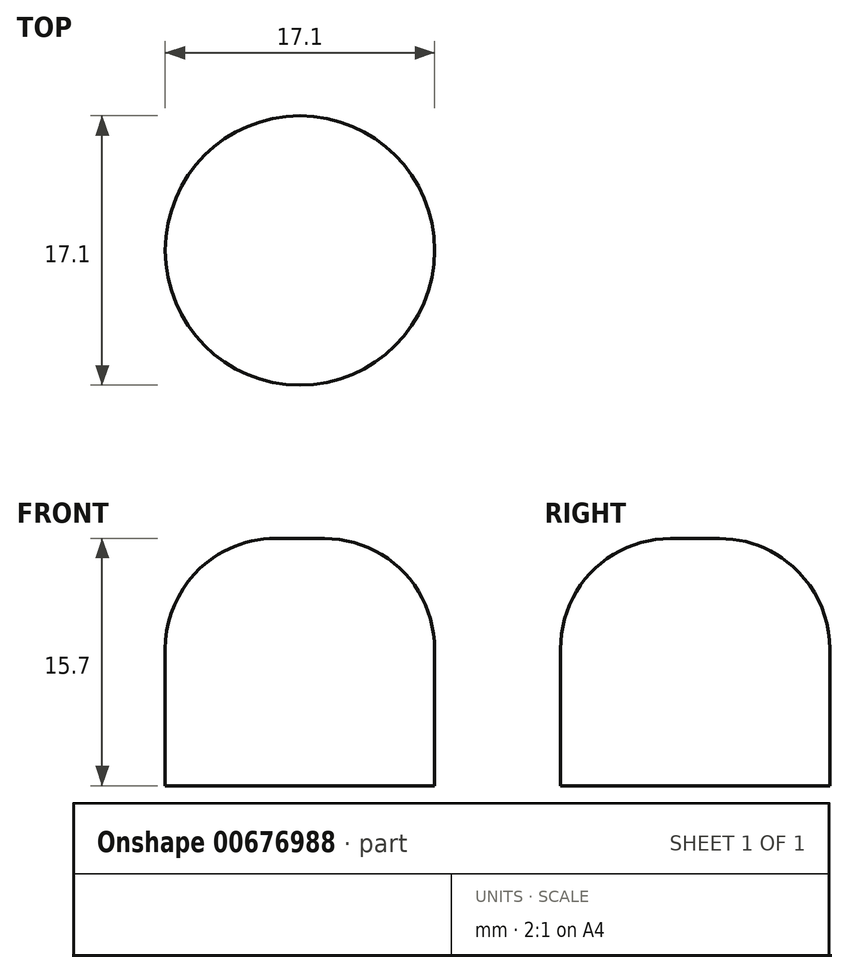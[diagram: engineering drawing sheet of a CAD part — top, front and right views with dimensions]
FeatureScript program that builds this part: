
annotation { "Feature Type Name" : "Feature", "Feature Type Description" : "" }
export const myFeature = defineFeature(function(context is Context, id is Id, definition is map)
    precondition{}
    {
        {
            var Q0;
            Q0=qCreatedBy(makeId("Top.planeOp"),FACE);
            var sketch = newSketch(context, id + "F0", { "sketchPlane" : qUnion([Q0])});
            skCircle(sketch, "E0", {"center": v(0, 0) * mm, "radius": 8.55 * mm});
            skSolve(sketch);
        }
        {
            var Q0;
            Q0 = qSketchRegion(id + "F0", true);
            extrude(context, id + "F1", {"entities" : qUnion([Q0]), "depth" : 8.7 * mm, "offsetDistance" : 25 * mm});
        }
        {
            var Q0;
            Q0=makeQuery(id+"F1.opExtrude","CAP_FACE",FACE,{"disambiguationData":[OSD([sQuery(id+"F0.wireOp",EDGE,"E0")])],"isStart":false});
            var sketch = newSketch(context, id + "F2", { "sketchPlane" : qUnion([Q0])});
            skSolve(sketch);
        }
        {
            var Q0;
            Q0=makeQuery(id+"F2.imprint","IMPRINT",FACE,{"disambiguationData":[TD([[makeQuery(id+"F2.imprint","IMPRINT",EDGE,{"derivedFrom":makeQuery(id+"F1.opExtrude","CAP_EDGE",EDGE,{"disambiguationData":[OSD([sQuery(id+"F0.wireOp",EDGE,"E0")])],"isStart":false})}),1.0]])]});
            var sketch = newSketch(context, id + "F3", { "sketchPlane" : qUnion([Q0])});
            skCircle(sketch, "E1", {"center": v(0, 0) * mm, "radius": 8.55 * mm});
            skSolve(sketch);
        }
        {
            var Q0;
            Q0 = qSketchRegion(id + "F3", true);
            extrude(context, id + "F4", {"entities" : qUnion([Q0]), "operationType" : NewBodyOperationType.ADD, "depth" : 7 * mm, "offsetDistance" : 25 * mm});
        }
        {
            var Q0;
            Q0=makeQuery(id+"F4.opExtrude","CAP_EDGE",EDGE,{"disambiguationData":[OSD([sQuery(id+"F3.wireOp",EDGE,"E1")])],"isStart":false});
            fillet(context, id + "F5", {"entities" : qUnion([Q0]), "radius" : 7 * mm, "tangentPropagation" : true, "allowEdgeOverflow" : false});
        }
    });
